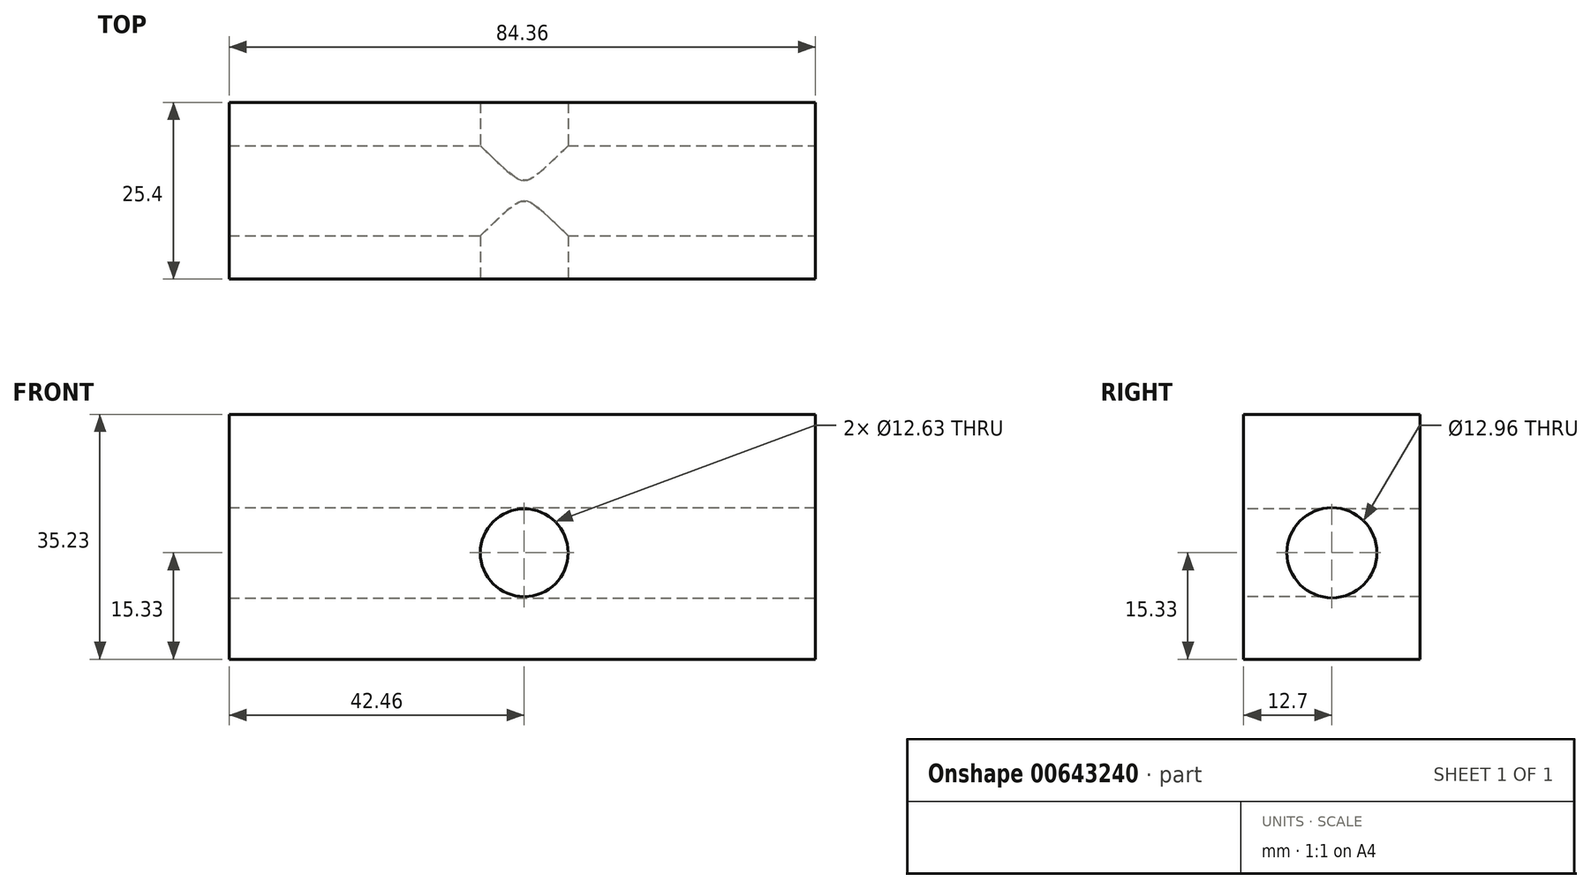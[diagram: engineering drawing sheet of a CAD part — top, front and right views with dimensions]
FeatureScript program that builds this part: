
annotation { "Feature Type Name" : "Feature", "Feature Type Description" : "" }
export const myFeature = defineFeature(function(context is Context, id is Id, definition is map)
    precondition{}
    {
        {
            var Q0;
            Q0=qCreatedBy(makeId("Front.planeOp"),FACE);
            var sketch = newSketch(context, id + "F0", { "sketchPlane" : qUnion([Q0])});
            skLineSegment(sketch, "E0.bottom", {"start": v(-42.46, 19.9) * mm, "end": v(41.9, 19.9) * mm});
            skLineSegment(sketch, "E0.top", {"start": v(-42.46, -15.33) * mm, "end": v(41.9, -15.33) * mm});
            skLineSegment(sketch, "E0.left", {"start": v(-42.46, 19.9) * mm, "end": v(-42.46, -15.33) * mm});
            skLineSegment(sketch, "E0.right", {"start": v(41.9, 19.9) * mm, "end": v(41.9, -15.33) * mm});
            skSolve(sketch);
        }
        {
            var Q0;
            Q0=makeQuery(id+"F0.imprint","IMPRINT",FACE,{"disambiguationData":[TD([[makeQuery(id+"F0.imprint","IMPRINT",EDGE,{"derivedFrom":sQuery(id+"F0.wireOp",EDGE,"E0.bottom")}),-1.0]])]});
            extrude(context, id + "F1", {"entities" : qUnion([Q0]), "depth" : 25.4 * mm, "offsetDistance" : 25.4 * mm});
        }
        {
            var Q0;
            Q0=makeQuery(id+"F1.opExtrude","CAP_FACE",FACE,{"disambiguationData":[OSD([sQuery(id+"F0.wireOp",EDGE,"E0.bottom"),sQuery(id+"F0.wireOp",EDGE,"E0.top"),sQuery(id+"F0.wireOp",EDGE,"E0.left"),sQuery(id+"F0.wireOp",EDGE,"E0.right")])],"isStart":false});
            var sketch = newSketch(context, id + "F2", { "sketchPlane" : qUnion([Q0])});
            skCircle(sketch, "E1", {"center": v(0, 0) * mm, "radius": 6.32 * mm});
            skSolve(sketch);
        }
        {
            var Q0;
            Q0 = qSketchRegion(id + "F2", true);
            extrude(context, id + "F3", {"entities" : qUnion([Q0]), "operationType" : NewBodyOperationType.REMOVE, "endBound" : BoundingType.THROUGH_ALL, "oppositeDirection" : true, "depth" : 25.4 * mm, "offsetDistance" : 25.4 * mm});
        }
        {
            var Q0;
            Q0=makeQuery(id+"F1.opExtrude","SWEPT_FACE",FACE,{"disambiguationData":[OSD([sQuery(id+"F0.wireOp",EDGE,"E0.right")])]});
            var sketch = newSketch(context, id + "F4", { "sketchPlane" : qUnion([Q0])});
            skCircle(sketch, "E2", {"center": v(-12.7, 0) * mm, "radius": 6.48 * mm});
            skPoint(sketch, "E2.centerSnap0", {"position": v(-12.7, 19.9) * mm});
            skSolve(sketch);
        }
        {
            var Q0;
            Q0=makeQuery(id+"F4.imprint","IMPRINT",FACE,{"disambiguationData":[TD([[makeQuery(id+"F4.imprint","IMPRINT",EDGE,{"derivedFrom":sQuery(id+"F4.wireOp",EDGE,"E2")}),1.0]])]});
            extrude(context, id + "F5", {"entities" : qUnion([Q0]), "operationType" : NewBodyOperationType.REMOVE, "endBound" : BoundingType.THROUGH_ALL, "oppositeDirection" : true, "depth" : 25.4 * mm, "offsetDistance" : 25.4 * mm});
        }
    });
